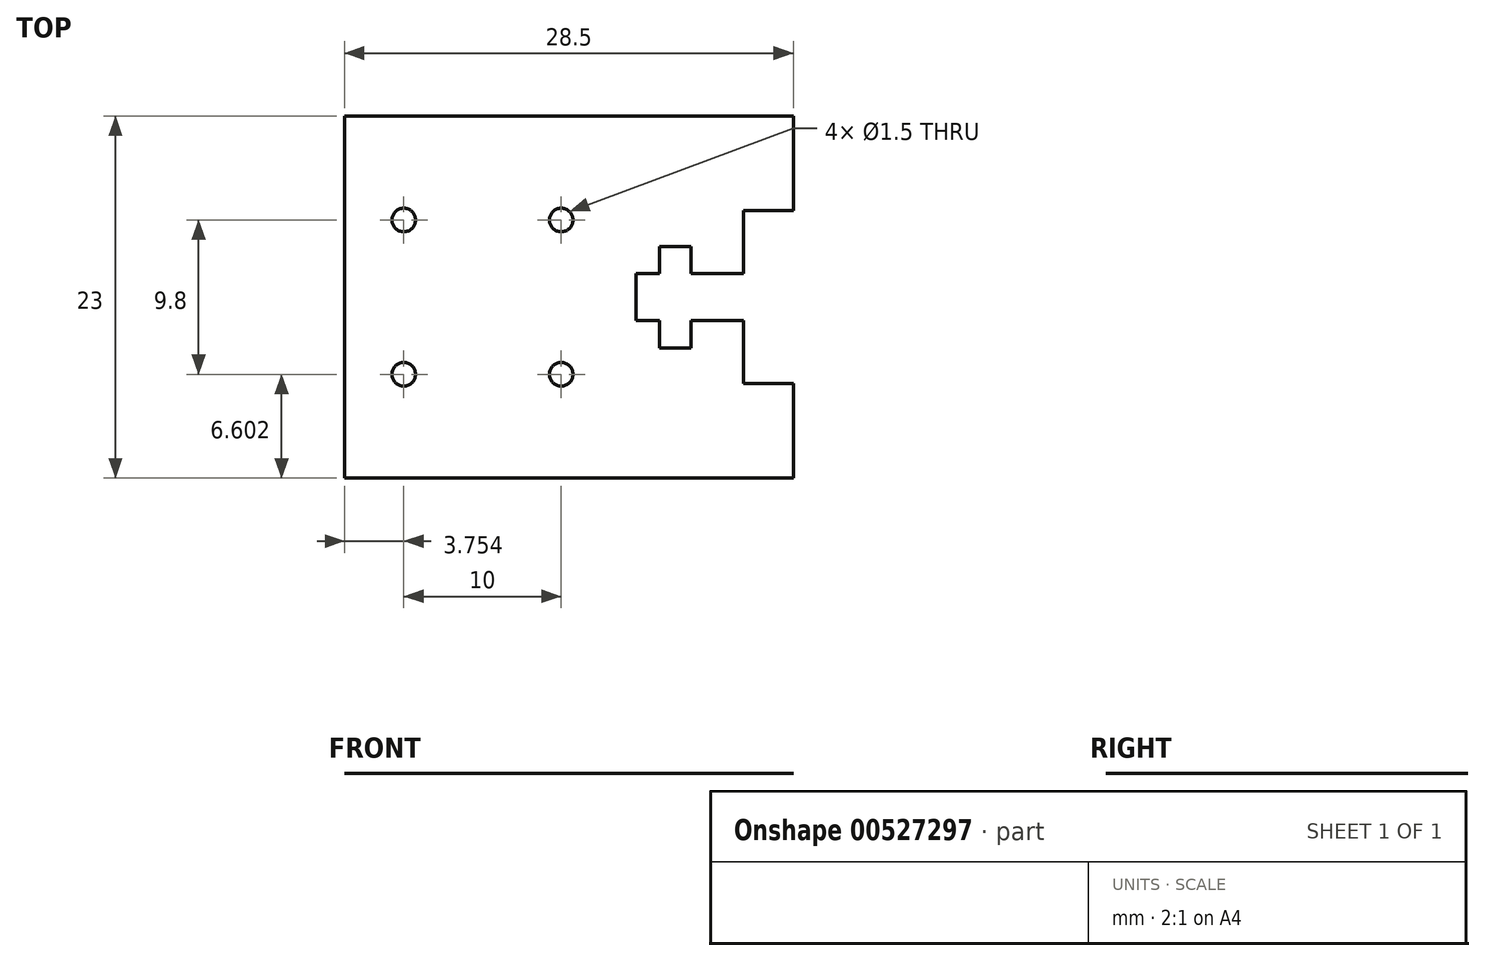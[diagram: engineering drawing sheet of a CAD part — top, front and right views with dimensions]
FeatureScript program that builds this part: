
annotation { "Feature Type Name" : "Feature", "Feature Type Description" : "" }
export const myFeature = defineFeature(function(context is Context, id is Id, definition is map)
    precondition{}
    {
        {
            var Q0;
            Q0=qCreatedBy(makeId("Top.planeOp"),FACE);
            var sketch = newSketch(context, id + "F0", { "sketchPlane" : qUnion([Q0])});
            skLineSegment(sketch, "E0.bottom", {"start": v(18.93, 10.4) * mm, "end": v(28.93, 10.4) * mm});
            skLineSegment(sketch, "E0.top", {"start": v(18.93, 7.4) * mm, "end": v(28.93, 7.4) * mm});
            skLineSegment(sketch, "E0.left", {"start": v(18.93, 10.4) * mm, "end": v(18.93, 7.4) * mm});
            skLineSegment(sketch, "E0.right", {"start": v(28.93, 10.4) * mm, "end": v(28.93, 7.4) * mm});
            skPoint(sketch, "E0.middle", {"position": v(23.93, 8.9) * mm});
            skLineSegment(sketch, "E1.bottom", {"start": v(20.43, 12.12) * mm, "end": v(22.43, 12.12) * mm});
            skLineSegment(sketch, "E1.top", {"start": v(20.43, 5.67) * mm, "end": v(22.43, 5.67) * mm});
            skLineSegment(sketch, "E1.left", {"start": v(20.43, 12.12) * mm, "end": v(20.43, 5.67) * mm});
            skLineSegment(sketch, "E1.right", {"start": v(22.43, 12.12) * mm, "end": v(22.43, 5.67) * mm});
            skPoint(sketch, "E1.middle", {"position": v(21.43, 8.9) * mm});
            skLineSegment(sketch, "E2", {"start": v(21.43, 8.9) * mm, "end": v(23.93, 8.9) * mm});
            skLineSegment(sketch, "E3.bottom", {"start": v(28.93, 14.4) * mm, "end": v(25.76, 14.4) * mm});
            skLineSegment(sketch, "E3.top", {"start": v(28.93, 20.4) * mm, "end": v(25.76, 20.4) * mm});
            skLineSegment(sketch, "E3.left", {"start": v(28.93, 14.4) * mm, "end": v(28.93, 20.4) * mm});
            skLineSegment(sketch, "E3.right", {"start": v(25.76, 14.4) * mm, "end": v(25.76, 20.4) * mm});
            skLineSegment(sketch, "E4.MirrorCS", {"start": v(25.76, 3.4) * mm, "end": v(25.76, -2.6) * mm});
            skLineSegment(sketch, "E5.MirrorCS", {"start": v(28.93, -2.6) * mm, "end": v(25.76, -2.6) * mm});
            skLineSegment(sketch, "E6.MirrorCS", {"start": v(28.93, 3.4) * mm, "end": v(28.93, -2.6) * mm});
            skLineSegment(sketch, "E7.MirrorCS", {"start": v(28.93, 3.4) * mm, "end": v(25.76, 3.4) * mm});
            skCircle(sketch, "E8", {"center": v(14.18, 13.8) * mm, "radius": 0.75 * mm});
            skLineSegment(sketch, "E9", {"start": v(9.18, 12.23) * mm, "end": v(9.18, 4.95) * mm});
            skCircle(sketch, "E10.MirrorC", {"center": v(4.18, 13.8) * mm, "radius": 0.75 * mm});
            skLineSegment(sketch, "E11.bottom", {"start": v(28.93, 20.4) * mm, "end": v(0.43, 20.4) * mm});
            skLineSegment(sketch, "E11.top", {"start": v(28.93, -2.6) * mm, "end": v(0.43, -2.6) * mm});
            skLineSegment(sketch, "E11.left", {"start": v(28.93, 20.4) * mm, "end": v(28.93, -2.6) * mm});
            skLineSegment(sketch, "E11.right", {"start": v(0.43, 20.4) * mm, "end": v(0.43, -2.6) * mm});
            skLineSegment(sketch, "E12", {"start": v(25.76, 14.4) * mm, "end": v(25.76, 3.4) * mm});
            skCircle(sketch, "E13", {"center": v(4.18, 4) * mm, "radius": 0.75 * mm});
            skCircle(sketch, "E14.MirrorC", {"center": v(14.18, 4) * mm, "radius": 0.75 * mm});
            skLineSegment(sketch, "E15", {"start": v(14.18, 13.8) * mm, "end": v(14.18, 4) * mm});
            skLineSegment(sketch, "E16", {"start": v(14.18, 8.9) * mm, "end": v(9.18, 8.9) * mm});
            skSolve(sketch);
        }
        {
            var Q0;
            {var subQ5=sQuery(id+"F0.wireOp",EDGE,"E0.left");Q0=makeQuery(id+"F0.imprint","IMPRINT",FACE,{"disambiguationData":[TD([[makeQuery(id+"F0.imprint","IMPRINT",EDGE,{"derivedFrom":subQ5}),-1.0]])]});}
            var Q1;
            {var subQ0=sQuery(id+"F0.wireOp",EDGE,"E3.bottom");Q1=makeQuery(id+"F0.imprint","IMPRINT",FACE,{"disambiguationData":[TD([[makeQuery(id+"F0.imprint","IMPRINT",EDGE,{"derivedFrom":subQ0}),-1.0]])]});}
            var Q2;
            {var subQ0=sQuery(id+"F0.wireOp",EDGE,"E4.MirrorCS");Q2=makeQuery(id+"F0.imprint","IMPRINT",FACE,{"disambiguationData":[TD([[makeQuery(id+"F0.imprint","IMPRINT",EDGE,{"derivedFrom":subQ0}),1.0]])]});}
            extrude(context, id + "F1", {"entities" : qUnion([Q0, Q1, Q2]), "depth" : 1 / 203.2 * mm, "offsetDistance" : 25 * mm});
        }
    });
